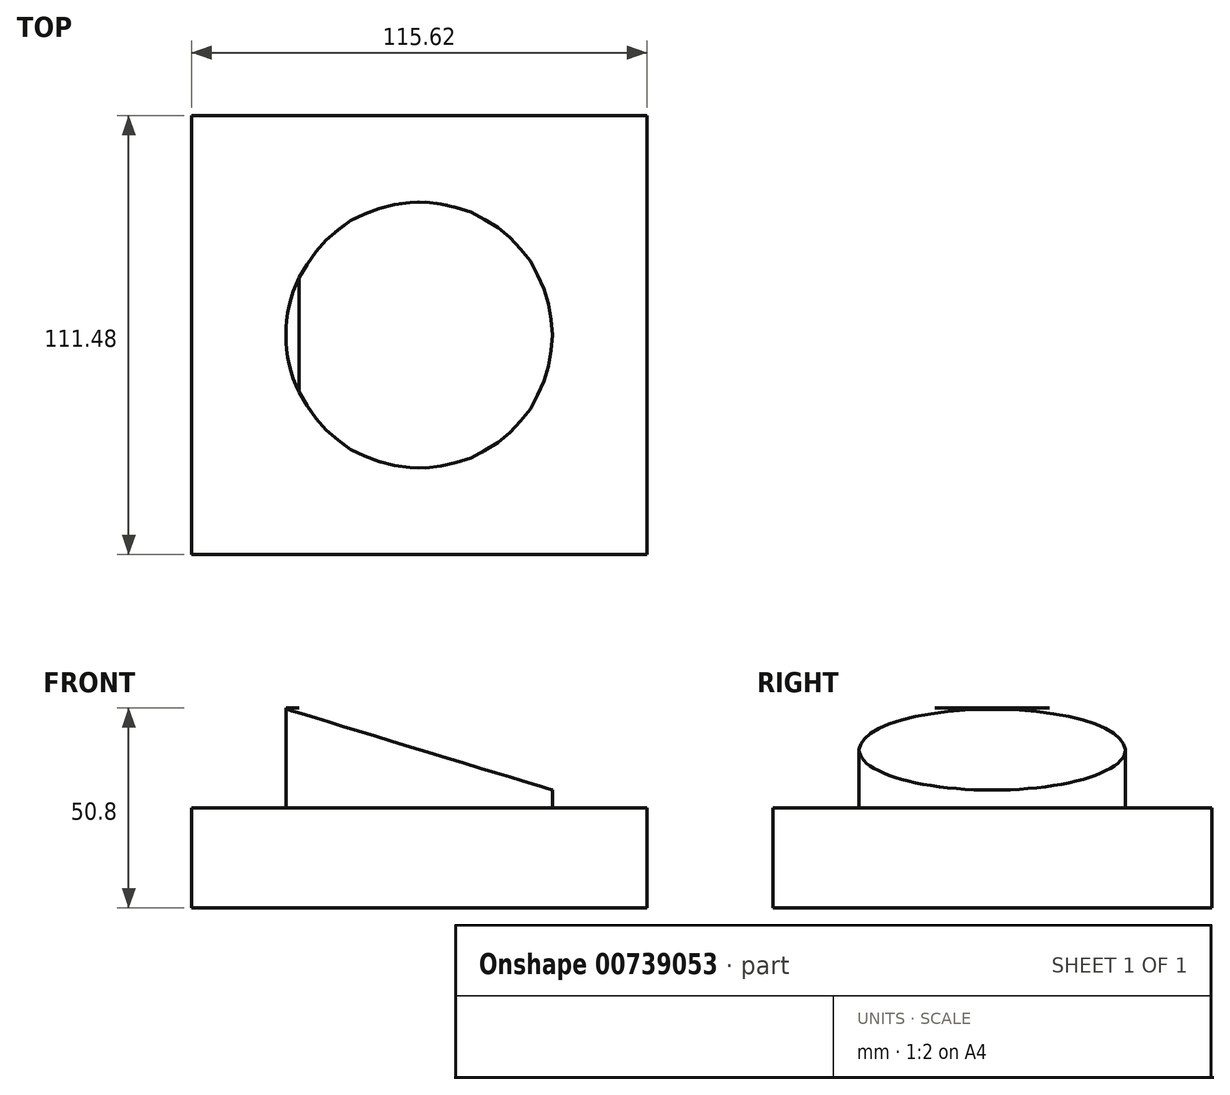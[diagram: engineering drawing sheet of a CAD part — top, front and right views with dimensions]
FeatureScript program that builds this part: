
annotation { "Feature Type Name" : "Feature", "Feature Type Description" : "" }
export const myFeature = defineFeature(function(context is Context, id is Id, definition is map)
    precondition{}
    {
        {
            var Q0;
            Q0=qCreatedBy(makeId("Top.planeOp"),FACE);
            var sketch = newSketch(context, id + "F0", { "sketchPlane" : qUnion([Q0])});
            skLineSegment(sketch, "E0.bottom", {"start": v(-57.81, 55.74) * mm, "end": v(57.81, 55.74) * mm});
            skLineSegment(sketch, "E0.top", {"start": v(-57.81, -55.74) * mm, "end": v(57.81, -55.74) * mm});
            skLineSegment(sketch, "E0.left", {"start": v(-57.81, 55.74) * mm, "end": v(-57.81, -55.74) * mm});
            skLineSegment(sketch, "E0.right", {"start": v(57.81, 55.74) * mm, "end": v(57.81, -55.74) * mm});
            skPoint(sketch, "E0.middle", {"position": v(0, 0) * mm});
            skSolve(sketch);
        }
        {
            var Q0;
            Q0 = qSketchRegion(id + "F0", true);
            extrude(context, id + "F1", {"entities" : qUnion([Q0]), "depth" : 25.4 * mm, "offsetDistance" : 25.4 * mm});
        }
        {
            var Q0;
            Q0=makeQuery(id+"F1.opExtrude","CAP_FACE",FACE,{"disambiguationData":[OSD([sQuery(id+"F0.wireOp",EDGE,"E0.bottom"),sQuery(id+"F0.wireOp",EDGE,"E0.top"),sQuery(id+"F0.wireOp",EDGE,"E0.left"),sQuery(id+"F0.wireOp",EDGE,"E0.right")])],"isStart":false});
            var sketch = newSketch(context, id + "F2", { "sketchPlane" : qUnion([Q0])});
            skCircle(sketch, "E1", {"center": v(0, 0) * mm, "radius": 33.88 * mm});
            skSolve(sketch);
        }
        {
            var Q0;
            Q0 = qSketchRegion(id + "F2", true);
            extrude(context, id + "F3", {"entities" : qUnion([Q0]), "operationType" : NewBodyOperationType.ADD, "depth" : 25.4 * mm, "offsetDistance" : 25.4 * mm});
        }
        {
            var Q0;
            Q0=qCreatedBy(makeId("Front.planeOp"),FACE);
            var sketch = newSketch(context, id + "F4", { "sketchPlane" : qUnion([Q0])});
            skLineSegment(sketch, "E2", {"start": v(-34.23, 50.62) * mm, "end": v(36.72, 29.04) * mm});
            skLineSegment(sketch, "E3", {"start": v(36.72, 29.04) * mm, "end": v(36.72, 54.15) * mm});
            skLineSegment(sketch, "E4", {"start": v(36.72, 54.15) * mm, "end": v(-34.23, 50.62) * mm});
            skSolve(sketch);
        }
        {
            var Q0;
            Q0=makeQuery(id+"F4.imprint","IMPRINT",FACE,{"disambiguationData":[TD([[makeQuery(id+"F4.imprint","IMPRINT",EDGE,{"derivedFrom":sQuery(id+"F4.wireOp",EDGE,"E2")}),1.0]])]});
            extrude(context, id + "F5", {"entities" : qUnion([Q0]), "operationType" : NewBodyOperationType.REMOVE, "depth" : 50.8 * mm, "offsetDistance" : 25.4 * mm, "hasSecondDirection" : true, "secondDirectionOppositeDirection" : true, "secondDirectionDepth" : 50.8 * mm});
        }
    });
